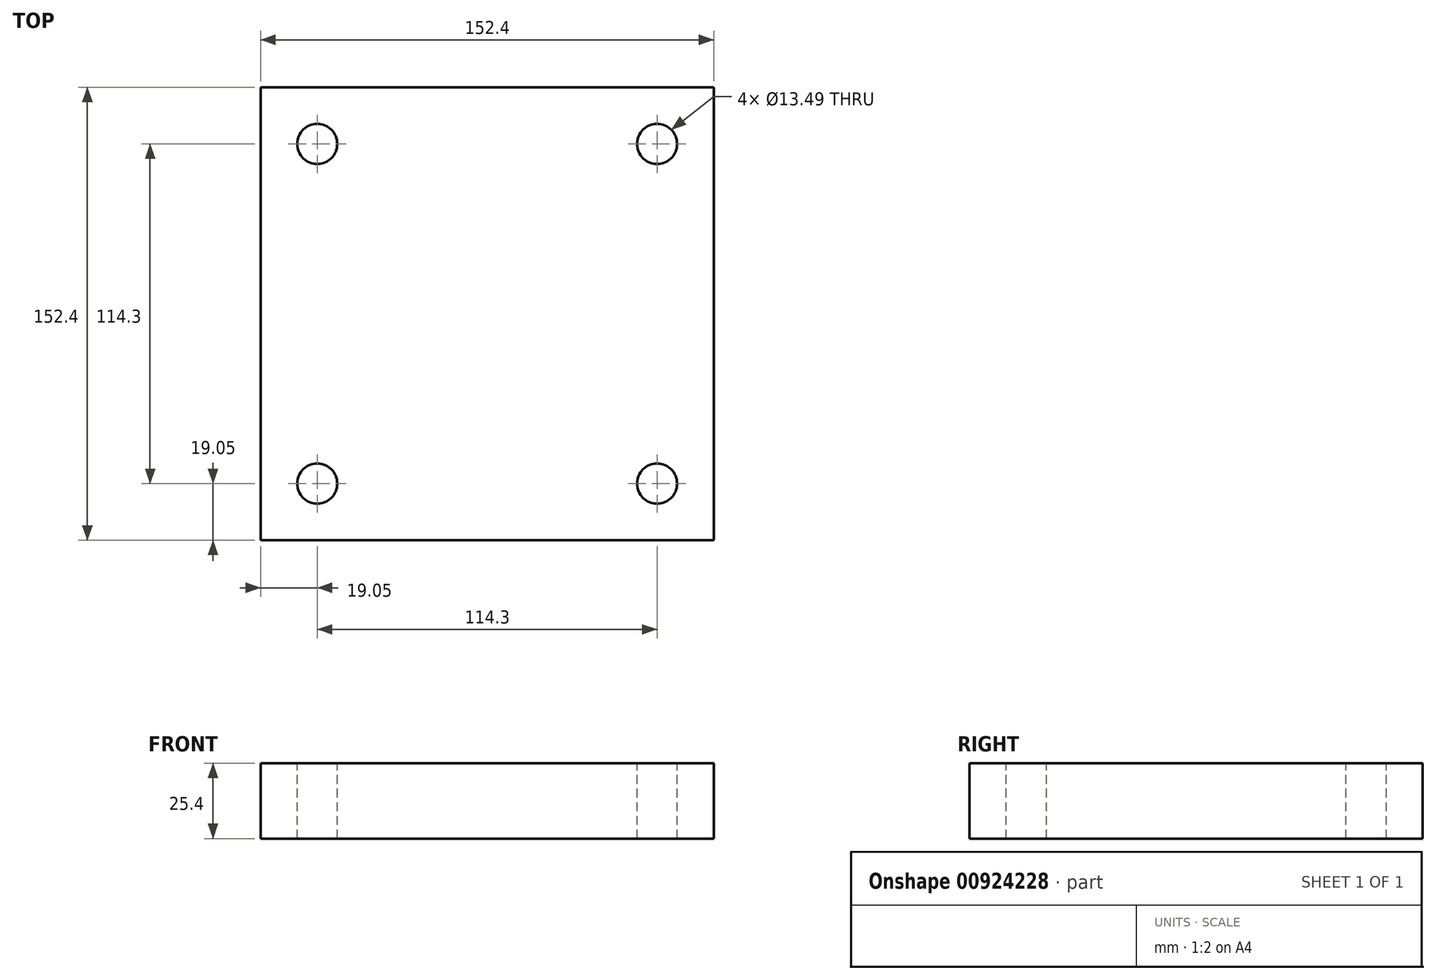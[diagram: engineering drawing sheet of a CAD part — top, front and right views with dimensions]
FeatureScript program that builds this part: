
annotation { "Feature Type Name" : "Feature", "Feature Type Description" : "" }
export const myFeature = defineFeature(function(context is Context, id is Id, definition is map)
    precondition{}
    {
        {
            var Q0;
            Q0=qCreatedBy(makeId("Top.planeOp"),FACE);
            var sketch = newSketch(context, id + "F0", { "sketchPlane" : qUnion([Q0])});
            skLineSegment(sketch, "E0.bottom", {"start": v(-76.2, 76.2) * mm, "end": v(76.2, 76.2) * mm});
            skLineSegment(sketch, "E0.top", {"start": v(-76.2, -76.2) * mm, "end": v(76.2, -76.2) * mm});
            skLineSegment(sketch, "E0.left", {"start": v(-76.2, 76.2) * mm, "end": v(-76.2, -76.2) * mm});
            skLineSegment(sketch, "E0.right", {"start": v(76.2, 76.2) * mm, "end": v(76.2, -76.2) * mm});
            skPoint(sketch, "E0.middle", {"position": v(0, 0) * mm});
            skSolve(sketch);
        }
        {
            var Q0;
            Q0=makeQuery(id+"F0.imprint","IMPRINT",FACE,{"disambiguationData":[TD([[makeQuery(id+"F0.imprint","IMPRINT",EDGE,{"derivedFrom":sQuery(id+"F0.wireOp",EDGE,"E0.bottom")}),-1.0]])]});
            extrude(context, id + "F1", {"entities" : qUnion([Q0]), "oppositeDirection" : true, "depth" : 25.4 * mm, "offsetDistance" : 25.4 * mm});
        }
        {
            var Q0;
            Q0=makeQuery(id+"F1.opExtrude","CAP_FACE",FACE,{"disambiguationData":[OSD([sQuery(id+"F0.wireOp",EDGE,"E0.bottom"),sQuery(id+"F0.wireOp",EDGE,"E0.top"),sQuery(id+"F0.wireOp",EDGE,"E0.left"),sQuery(id+"F0.wireOp",EDGE,"E0.right")])],"isStart":true});
            var sketch = newSketch(context, id + "F2", { "sketchPlane" : qUnion([Q0])});
            skLineSegment(sketch, "E1.bottom", {"start": v(-57.15, 57.15) * mm, "end": v(57.15, 57.15) * mm, "construction": true});
            skLineSegment(sketch, "E1.top", {"start": v(-57.15, -57.15) * mm, "end": v(57.15, -57.15) * mm, "construction": true});
            skLineSegment(sketch, "E1.left", {"start": v(-57.15, 57.15) * mm, "end": v(-57.15, -57.15) * mm, "construction": true});
            skLineSegment(sketch, "E1.right", {"start": v(57.15, 57.15) * mm, "end": v(57.15, -57.15) * mm, "construction": true});
            skPoint(sketch, "E1.middle", {"position": v(0, 0) * mm});
            skPoint(sketch, "E2", {"position": v(-57.15, 57.15) * mm});
            skPoint(sketch, "E3", {"position": v(57.15, 57.15) * mm});
            skPoint(sketch, "E4", {"position": v(-57.15, -57.15) * mm});
            skPoint(sketch, "E5", {"position": v(57.15, -57.15) * mm});
            skSolve(sketch);
        }
        {
            var Q0;
            Q0=sQuery(id+"F2.wireOp",VERTEX,"E2");
            var Q1;
            Q1=sQuery(id+"F2.wireOp",VERTEX,"E3");
            var Q2;
            Q2=sQuery(id+"F2.wireOp",VERTEX,"E4");
            var Q3;
            Q3=sQuery(id+"F2.wireOp",VERTEX,"E5");
            var Q4;
            Q4=makeQuery(id+"F1.opExtrude","SWEPT_BODY",BODY,{"disambiguationData":[OSD([sQuery(id+"F0.wireOp",EDGE,"E0.bottom"),sQuery(id+"F0.wireOp",EDGE,"E0.top"),sQuery(id+"F0.wireOp",EDGE,"E0.left"),sQuery(id+"F0.wireOp",EDGE,"E0.right")])]});
            hole(context, id + "F3", {"style" : HoleStyle.SIMPLE, "endStyle" : HoleEndStyle.THROUGH, "standardTappedOrClearance" : lookupTablePath({ "standard" : "ANSI", "engagement" : "75%", "pitch" : "11 tpi", "size" : "5/8", "type" : "Tapped" }), "standardBlindInLast" : lookupTablePath({ "standard" : "ANSI", "engagement" : "75%", "pitch" : "11 tpi", "size" : "5/8", "type" : "Tapped" }), "holeDiameter" : 13.5 * mm, "majorDiameter" : 15.88 * mm, "showTappedDepth" : true, "isTappedThrough" : true, "tappedDepth" : 7.9 * mm, "tapClearance" : 3, "startFromSketch" : true, "locations" : qUnion([Q0, Q1, Q2, Q3]), "scope" : qUnion([Q4])});
        }
    });
